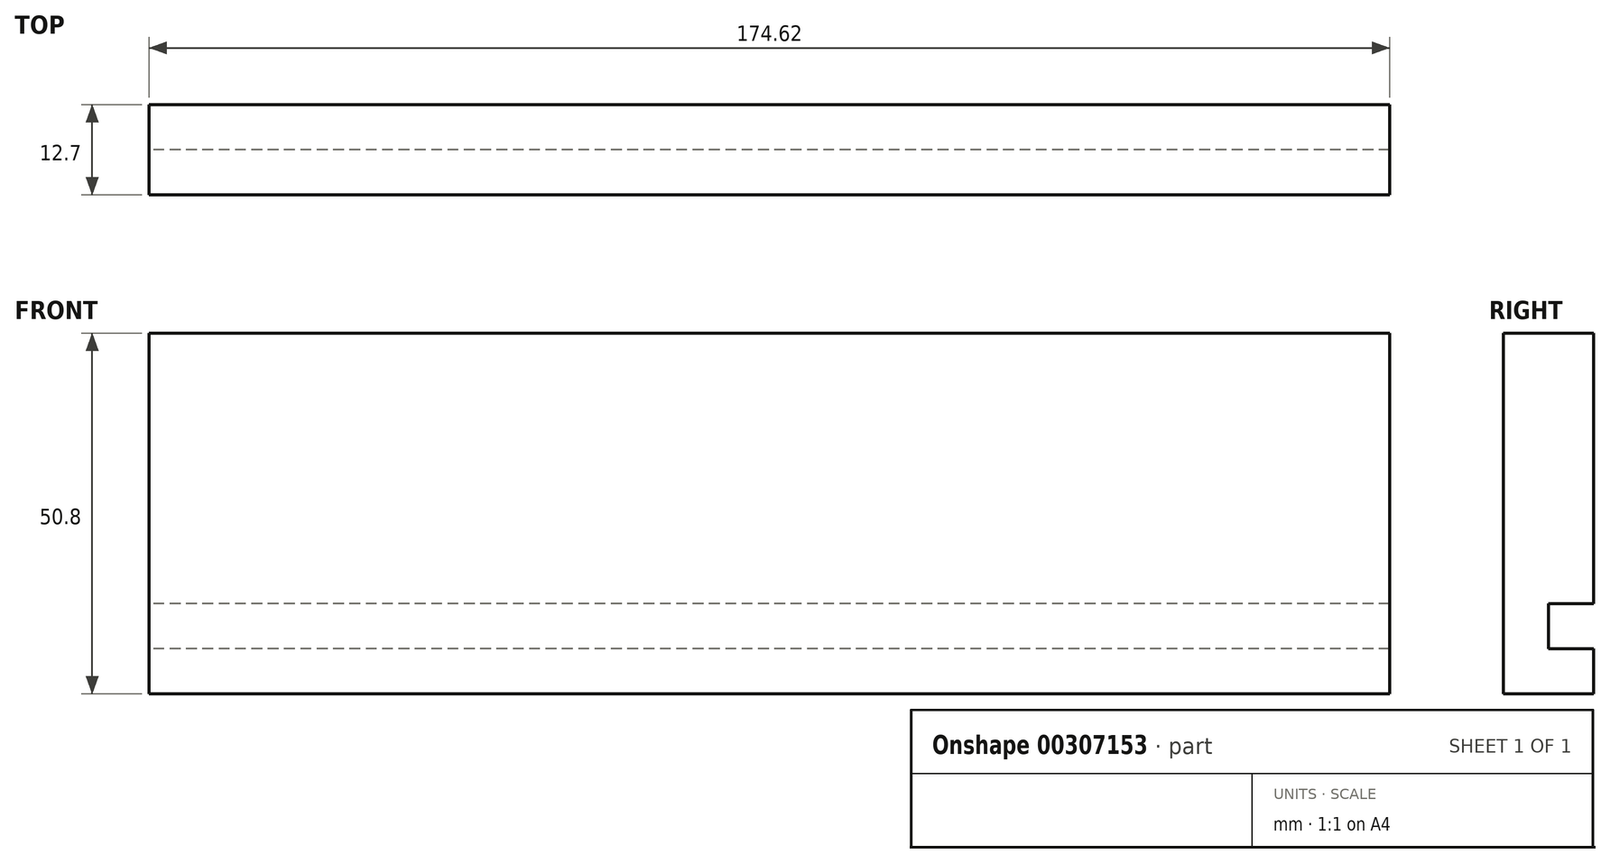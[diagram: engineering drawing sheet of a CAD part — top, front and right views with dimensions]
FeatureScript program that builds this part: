
annotation { "Feature Type Name" : "Feature", "Feature Type Description" : "" }
export const myFeature = defineFeature(function(context is Context, id is Id, definition is map)
    precondition{}
    {
        {
            var Q0;
            Q0=qCreatedBy(makeId("Front.planeOp"),FACE);
            var sketch = newSketch(context, id + "F0", { "sketchPlane" : qUnion([Q0])});
            skLineSegment(sketch, "E0.bottom", {"start": v(87.31, -25.4) * mm, "end": v(-87.31, -25.4) * mm});
            skLineSegment(sketch, "E0.top", {"start": v(87.31, 25.4) * mm, "end": v(-87.31, 25.4) * mm});
            skLineSegment(sketch, "E0.left", {"start": v(87.31, -25.4) * mm, "end": v(87.31, 25.4) * mm});
            skLineSegment(sketch, "E0.right", {"start": v(-87.31, -25.4) * mm, "end": v(-87.31, 25.4) * mm});
            skPoint(sketch, "E0.middle", {"position": v(0, 0) * mm});
            skSolve(sketch);
        }
        {
            var Q0;
            Q0=makeQuery(id+"F0.imprint","IMPRINT",FACE,{"disambiguationData":[TD([[makeQuery(id+"F0.imprint","IMPRINT",EDGE,{"derivedFrom":sQuery(id+"F0.wireOp",EDGE,"E0.bottom")}),-1.0]])]});
            extrude(context, id + "F1", {"entities" : qUnion([Q0]), "depth" : 12.7 * mm});
        }
        {
            var Q0;
            Q0=makeQuery(id+"F1.opExtrude","SWEPT_FACE",FACE,{"disambiguationData":[OSD([sQuery(id+"F0.wireOp",EDGE,"E0.right")])]});
            var sketch = newSketch(context, id + "F2", { "sketchPlane" : qUnion([Q0])});
            skLineSegment(sketch, "E1", {"start": v(0, -12.7) * mm, "end": v(6.35, -12.7) * mm});
            skLineSegment(sketch, "E2", {"start": v(6.35, -12.7) * mm, "end": v(6.35, -19.05) * mm});
            skLineSegment(sketch, "E3", {"start": v(6.35, -19.05) * mm, "end": v(0, -19.05) * mm});
            skSolve(sketch);
        }
        {
            var Q0;
            {var subQ0=sQuery(id+"F2.wireOp",EDGE,"E1");Q0=makeQuery(id+"F2.imprint","IMPRINT",FACE,{"disambiguationData":[TD([[makeQuery(id+"F2.imprint","IMPRINT",EDGE,{"derivedFrom":subQ0}),-1.0]])]});}
            extrude(context, id + "F3", {"entities" : qUnion([Q0]), "operationType" : NewBodyOperationType.REMOVE, "endBound" : BoundingType.THROUGH_ALL, "oppositeDirection" : true, "depth" : 25.4 * mm});
        }
    });
